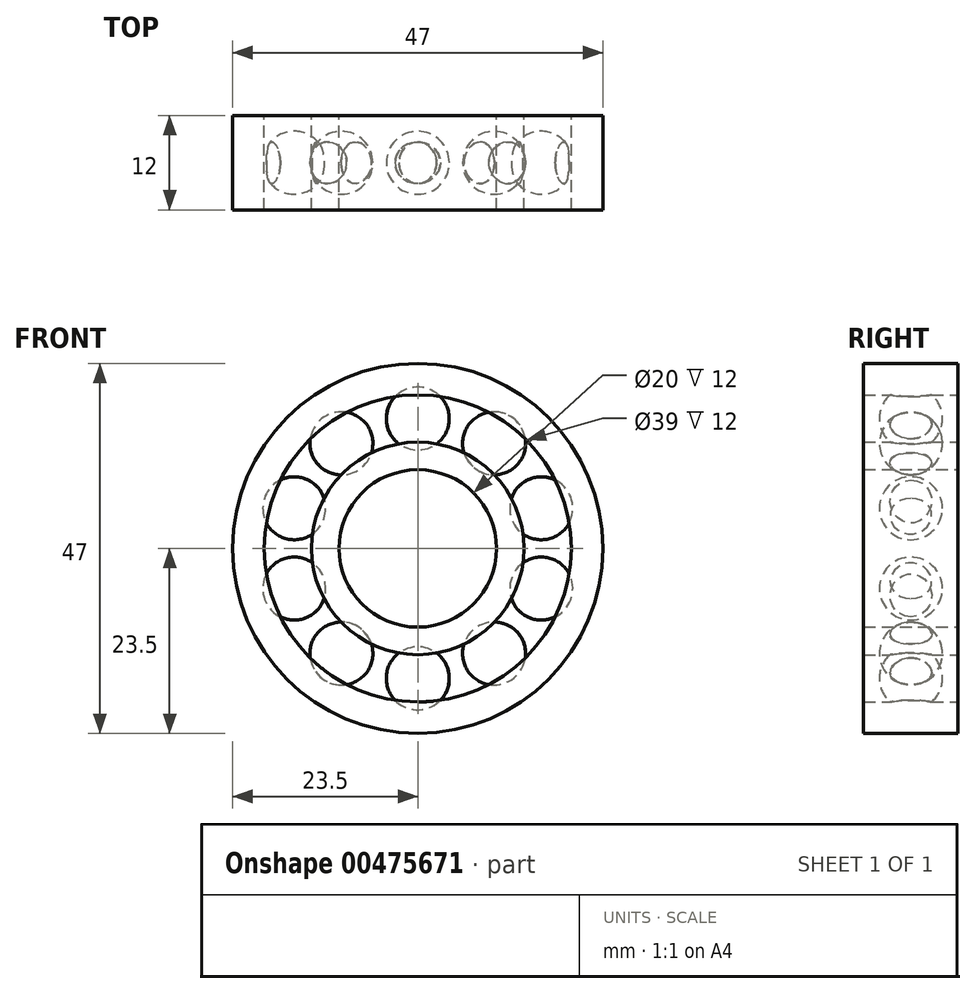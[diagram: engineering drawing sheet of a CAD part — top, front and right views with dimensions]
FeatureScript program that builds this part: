
annotation { "Feature Type Name" : "Feature", "Feature Type Description" : "" }
export const myFeature = defineFeature(function(context is Context, id is Id, definition is map)
    precondition{}
    {
        {
            var Q0;
            Q0=qCreatedBy(makeId("Front.planeOp"),FACE);
            var sketch = newSketch(context, id + "F0", { "sketchPlane" : qUnion([Q0])});
            skCircle(sketch, "E0", {"center": v(0, 0) * mm, "radius": 10 * mm});
            skCircle(sketch, "E1", {"center": v(0, 0) * mm, "radius": 13.5 * mm});
            skSolve(sketch);
        }
        {
            var Q0;
            Q0=makeQuery(id+"F0.imprint","IMPRINT",FACE,{"disambiguationData":[TD([[makeQuery(id+"F0.imprint","IMPRINT",EDGE,{"derivedFrom":sQuery(id+"F0.wireOp",EDGE,"E0")}),-1.0]])]});
            extrude(context, id + "F1", {"entities" : qUnion([Q0]), "depth" : 12 * mm});
        }
        {
            var Q0;
            Q0=qCreatedBy(makeId("Front.planeOp"),FACE);
            var sketch = newSketch(context, id + "F2", { "sketchPlane" : qUnion([Q0])});
            skCircle(sketch, "E2", {"center": v(0, 0) * mm, "radius": 19.5 * mm});
            skCircle(sketch, "E3", {"center": v(0, 0) * mm, "radius": 23.5 * mm});
            skSolve(sketch);
        }
        {
            var Q0;
            Q0=makeQuery(id+"F2.imprint","IMPRINT",FACE,{"disambiguationData":[TD([[makeQuery(id+"F2.imprint","IMPRINT",EDGE,{"derivedFrom":sQuery(id+"F2.wireOp",EDGE,"E2")}),-1.0]])]});
            extrude(context, id + "F3", {"entities" : qUnion([Q0]), "depth" : 12 * mm});
        }
        {
            var Q0;
            Q0=qCreatedBy(makeId("Front.planeOp"),FACE);
            cPlane(context, id + "F4", {"entities" : qUnion([Q0]), "cplaneType" : CPlaneType.OFFSET, "offset" : 6 * mm, "width" : 150 * mm, "height" : 150 * mm});
        }
        {
            var Q0;
            Q0=qCreatedBy(id+"F4.planeOp",FACE);
            var sketch = newSketch(context, id + "F5", { "sketchPlane" : qUnion([Q0])});
            skArc(sketch, "E4", {"start": v(0, 12.5) * mm, "mid": v(4, 16.5) * mm, "end": v(0, 20.5) * mm});
            skLineSegment(sketch, "E5", {"start": v(0, 20.5) * mm, "end": v(0, 12.5) * mm});
            skPoint(sketch, "E6.orphan", {"position": v(0, 24.4) * mm});
            skSolve(sketch);
        }
        {
            var Q0;
            Q0 = qSketchRegion(id + "F5", true);
            var Q1;
            Q1=sQuery(id+"F5.wireOp",EDGE,"E5");
            revolve(context, id + "F6", {"entities" : qUnion([Q0]), "axis" : qUnion([Q1]), "revolveType" : RevolveType.FULL});
        }
        {
            var Q0;
            Q0=qCreatedBy(makeId("Right.planeOp"),FACE);
            var sketch = newSketch(context, id + "F7", { "sketchPlane" : qUnion([Q0])});
            skLineSegment(sketch, "E7", {"start": v(0, 0) * mm, "end": v(-140.5, 0) * mm, "construction": true});
            skSolve(sketch);
        }
        {
            var Q0;
            Q0=makeQuery(id+"F6.opRevolve","SWEPT_BODY",BODY,{"disambiguationData":[OSD([sQuery(id+"F5.wireOp",EDGE,"E4"),sQuery(id+"F5.wireOp",EDGE,"E5")])]});
            var Q1;
            Q1=sQuery(id+"F7.wireOp",EDGE,"E7");
            circularPattern(context, id + "F8", {"operationType" : NewBodyOperationType.ADD, "entities" : qUnion([Q0]), "axis" : qUnion([Q1]), "angle" : 360 * degree, "instanceCount" : 10, "equalSpace" : true});
        }
    });
